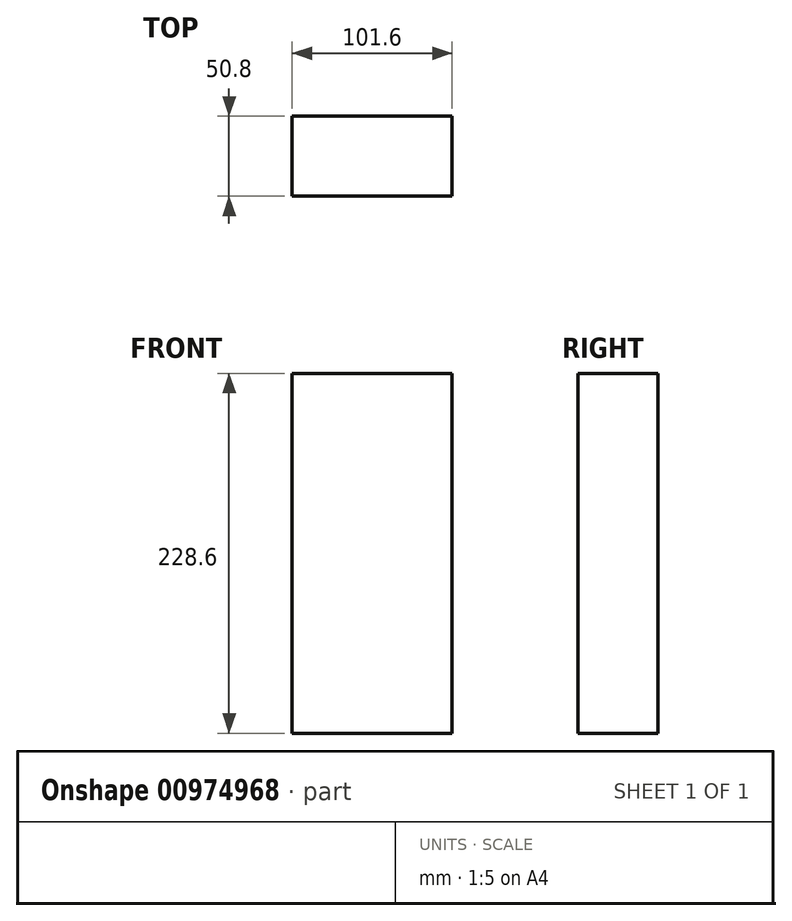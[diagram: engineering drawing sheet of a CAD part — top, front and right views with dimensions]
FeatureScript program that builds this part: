
annotation { "Feature Type Name" : "Feature", "Feature Type Description" : "" }
export const myFeature = defineFeature(function(context is Context, id is Id, definition is map)
    precondition{}
    {
        {
            var Q0;
            Q0=qCreatedBy(makeId("Front.planeOp"),FACE);
            var sketch = newSketch(context, id + "F0", { "sketchPlane" : qUnion([Q0])});
            skLineSegment(sketch, "E0.bottom", {"start": v(-53.1, 67.76) * mm, "end": v(48.5, 67.76) * mm});
            skLineSegment(sketch, "E0.top", {"start": v(-53.1, -160.84) * mm, "end": v(48.5, -160.84) * mm});
            skLineSegment(sketch, "E0.left", {"start": v(-53.1, 67.76) * mm, "end": v(-53.1, -160.84) * mm});
            skLineSegment(sketch, "E0.right", {"start": v(48.5, 67.76) * mm, "end": v(48.5, -160.84) * mm});
            skSolve(sketch);
        }
        {
            var Q0;
            Q0=makeQuery(id+"F0.imprint","IMPRINT",FACE,{"disambiguationData":[TD([[makeQuery(id+"F0.imprint","IMPRINT",EDGE,{"derivedFrom":sQuery(id+"F0.wireOp",EDGE,"E0.bottom")}),-1.0]])]});
            extrude(context, id + "F1", {"entities" : qUnion([Q0]), "depth" : 50.8 * mm, "offsetDistance" : 25.4 * mm});
        }
    });
